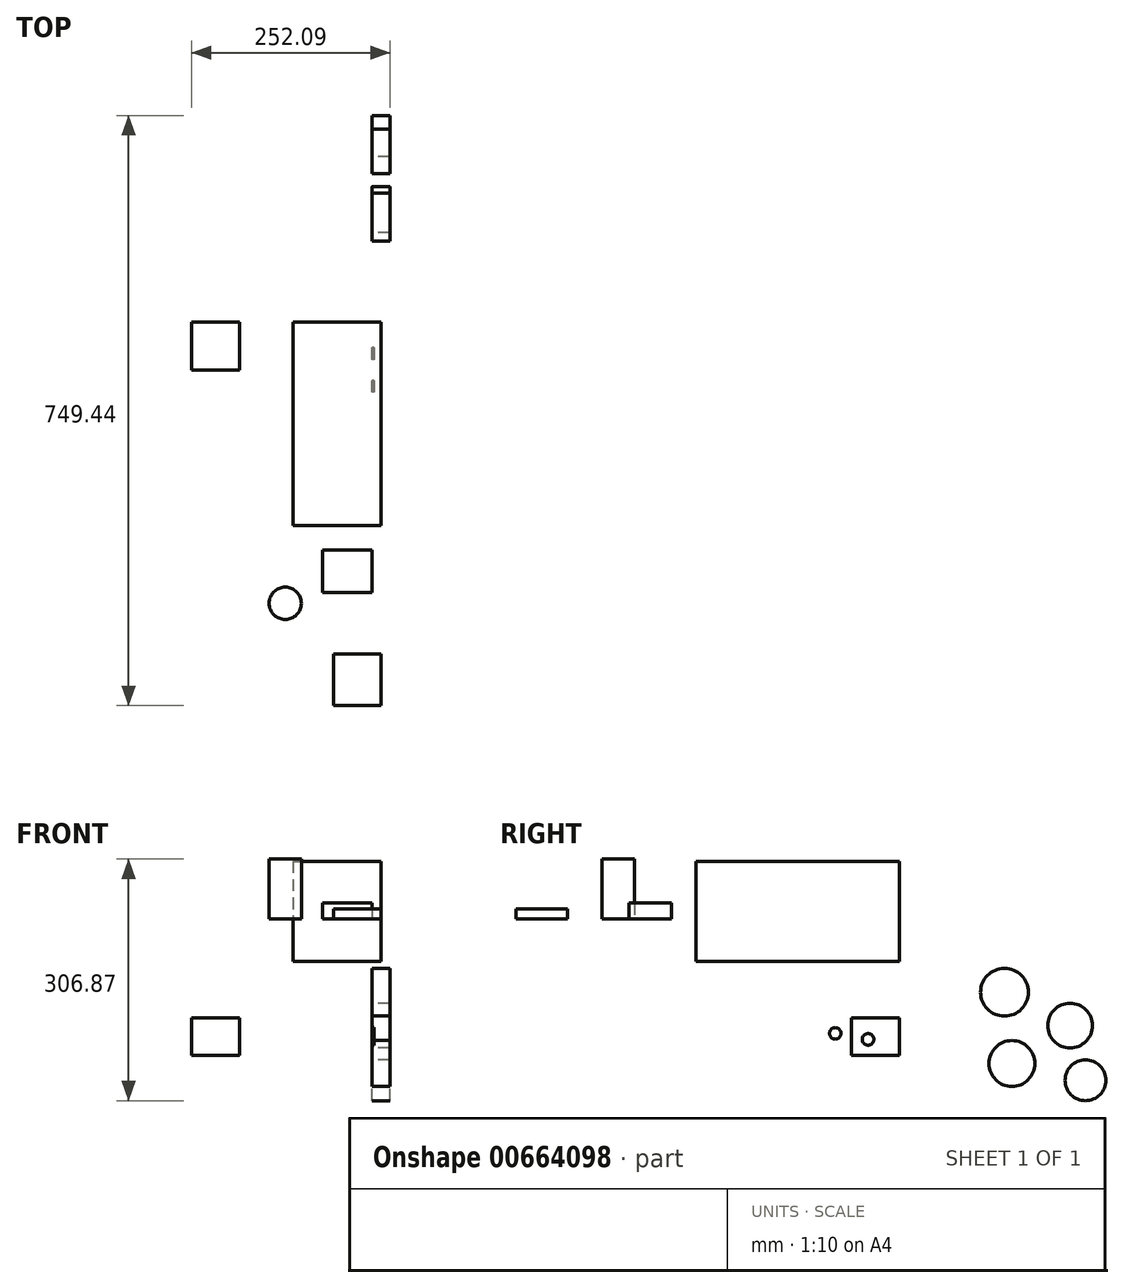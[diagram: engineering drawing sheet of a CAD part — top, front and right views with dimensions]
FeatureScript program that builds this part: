
annotation { "Feature Type Name" : "Feature", "Feature Type Description" : "" }
export const myFeature = defineFeature(function(context is Context, id is Id, definition is map)
    precondition{}
    {
        {
            var Q0;
            Q0=qCreatedBy(makeId("Front.planeOp"),FACE);
            var sketch = newSketch(context, id + "F0", { "sketchPlane" : qUnion([Q0])});
            skLineSegment(sketch, "E0.bottom", {"start": v(-100, 73.53) * mm, "end": v(11.53, 73.53) * mm});
            skLineSegment(sketch, "E0.top", {"start": v(-100, -53.5) * mm, "end": v(11.53, -53.5) * mm});
            skLineSegment(sketch, "E0.left", {"start": v(-100, 73.53) * mm, "end": v(-100, -53.5) * mm});
            skLineSegment(sketch, "E0.right", {"start": v(11.53, 73.53) * mm, "end": v(11.53, -53.5) * mm});
            skSolve(sketch);
        }
        {
            var Q0;
            Q0=makeQuery(id+"F0.imprint","IMPRINT",FACE,{"disambiguationData":[TD([[makeQuery(id+"F0.imprint","IMPRINT",EDGE,{"derivedFrom":sQuery(id+"F0.wireOp",EDGE,"E0.bottom")}),-1.0]])]});
            extrude(context, id + "F1", {"entities" : qUnion([Q0]), "depth" : 258.57 * mm, "offsetDistance" : 25.4 * mm});
        }
        {
            var Q0;
            Q0=qCreatedBy(makeId("Top.planeOp"),FACE);
            var sketch = newSketch(context, id + "F2", { "sketchPlane" : qUnion([Q0])});
            skLineSegment(sketch, "E1.bottom", {"start": v(-62.54, -289.87) * mm, "end": v(0, -289.87) * mm});
            skLineSegment(sketch, "E1.top", {"start": v(-62.54, -343.9) * mm, "end": v(0, -343.9) * mm});
            skLineSegment(sketch, "E1.left", {"start": v(-62.54, -289.87) * mm, "end": v(-62.54, -343.9) * mm});
            skLineSegment(sketch, "E1.right", {"start": v(0, -289.87) * mm, "end": v(0, -343.9) * mm});
            skSolve(sketch);
        }
        {
            var Q0;
            Q0=makeQuery(id+"F2.imprint","IMPRINT",FACE,{"disambiguationData":[TD([[makeQuery(id+"F2.imprint","IMPRINT",EDGE,{"derivedFrom":sQuery(id+"F2.wireOp",EDGE,"E1.bottom")}),-1.0]])]});
            extrude(context, id + "F3", {"entities" : qUnion([Q0]), "depth" : 20.32 * mm, "offsetDistance" : 25.4 * mm});
        }
        {
            var Q0;
            Q0=qCreatedBy(makeId("Front.planeOp"),FACE);
            var sketch = newSketch(context, id + "F4", { "sketchPlane" : qUnion([Q0])});
            skLineSegment(sketch, "E2.bottom", {"start": v(-167.87, -173.18) * mm, "end": v(-229.23, -173.18) * mm});
            skLineSegment(sketch, "E2.top", {"start": v(-167.87, -125.55) * mm, "end": v(-229.23, -125.55) * mm});
            skLineSegment(sketch, "E2.left", {"start": v(-167.87, -173.18) * mm, "end": v(-167.87, -125.55) * mm});
            skLineSegment(sketch, "E2.right", {"start": v(-229.23, -173.18) * mm, "end": v(-229.23, -125.55) * mm});
            skSolve(sketch);
        }
        {
            var Q0;
            Q0 = qSketchRegion(id + "F4", true);
            extrude(context, id + "F5", {"entities" : qUnion([Q0]), "depth" : 60.96 * mm, "offsetDistance" : 25.4 * mm});
        }
        {
            var Q0;
            Q0=qCreatedBy(makeId("Right.planeOp"),FACE);
            var sketch = newSketch(context, id + "F6", { "sketchPlane" : qUnion([Q0])});
            skCircle(sketch, "E3", {"center": v(216.52, -135.3) * mm, "radius": 28.38 * mm});
            skCircle(sketch, "E4", {"center": v(236.1, -204.76) * mm, "radius": 25.92 * mm});
            skCircle(sketch, "E5", {"center": v(142.61, -183.45) * mm, "radius": 29.15 * mm});
            skCircle(sketch, "E6", {"center": v(133.14, -92.92) * mm, "radius": 30.34 * mm});
            skSolve(sketch);
        }
        {
            var Q0;
            Q0 = qSketchRegion(id + "F6", true);
            extrude(context, id + "F7", {"entities" : qUnion([Q0]), "depth" : 22.86 * mm, "offsetDistance" : 25.4 * mm});
        }
        {
            var Q0;
            Q0=qCreatedBy(makeId("Right.planeOp"),FACE);
            var sketch = newSketch(context, id + "F8", { "sketchPlane" : qUnion([Q0])});
            skCircle(sketch, "E7", {"center": v(-81.83, -145.2) * mm, "radius": 7.33 * mm});
            skSolve(sketch);
        }
        {
            var Q0;
            Q0 = qSketchRegion(id + "F8", true);
            extrude(context, id + "F9", {"entities" : qUnion([Q0]), "depth" : 2.54 * mm, "offsetDistance" : 25.4 * mm});
        }
        {
            var Q0;
            Q0=qCreatedBy(makeId("Right.planeOp"),FACE);
            var sketch = newSketch(context, id + "F10", { "sketchPlane" : qUnion([Q0])});
            skCircle(sketch, "E8", {"center": v(-40.14, -152.8) * mm, "radius": 7.43 * mm});
            skSolve(sketch);
        }
        {
            var Q0;
            Q0 = qSketchRegion(id + "F10", true);
            extrude(context, id + "F11", {"entities" : qUnion([Q0]), "depth" : 2.54 * mm, "offsetDistance" : 25.4 * mm});
        }
        {
            var Q0;
            Q0=qCreatedBy(makeId("Top.planeOp"),FACE);
            var sketch = newSketch(context, id + "F12", { "sketchPlane" : qUnion([Q0])});
            skCircle(sketch, "E9", {"center": v(-110.19, -357.5) * mm, "radius": 20.53 * mm});
            skSolve(sketch);
        }
        {
            var Q0;
            Q0=makeQuery(id+"F12.imprint","IMPRINT",FACE,{"disambiguationData":[TD([[makeQuery(id+"F12.imprint","IMPRINT",EDGE,{"derivedFrom":sQuery(id+"F12.wireOp",EDGE,"E9")}),1.0]])]});
            extrude(context, id + "F13", {"entities" : qUnion([Q0]), "depth" : 76.2 * mm, "offsetDistance" : 25.4 * mm});
        }
        {
            var Q0;
            Q0=qCreatedBy(makeId("Top.planeOp"),FACE);
            var sketch = newSketch(context, id + "F14", { "sketchPlane" : qUnion([Q0])});
            skLineSegment(sketch, "E10.bottom", {"start": v(-48.74, -422.1) * mm, "end": v(11.4, -422.1) * mm});
            skLineSegment(sketch, "E10.top", {"start": v(-48.74, -487.43) * mm, "end": v(11.4, -487.43) * mm});
            skLineSegment(sketch, "E10.left", {"start": v(-48.74, -422.1) * mm, "end": v(-48.74, -487.43) * mm});
            skLineSegment(sketch, "E10.right", {"start": v(11.4, -422.1) * mm, "end": v(11.4, -487.43) * mm});
            skSolve(sketch);
        }
        {
            var Q0;
            Q0=makeQuery(id+"F14.imprint","IMPRINT",FACE,{"disambiguationData":[TD([[makeQuery(id+"F14.imprint","IMPRINT",EDGE,{"derivedFrom":sQuery(id+"F14.wireOp",EDGE,"E10.bottom")}),-1.0]])]});
            extrude(context, id + "F15", {"entities" : qUnion([Q0]), "depth" : 12.7 * mm, "offsetDistance" : 25.4 * mm});
        }
    });
